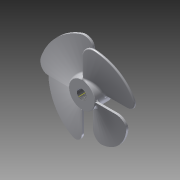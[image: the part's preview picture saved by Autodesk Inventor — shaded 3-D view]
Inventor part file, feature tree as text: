
AUTODESK INVENTOR PART (.ipt)
format: ipt  version: 2015 (Build 190159000, 159)  size: 707,584 bytes
history: native  units: mm
features: fillet x3, chamfer x2, sketch x2, extrude x1, helix x1, pattern_circular x1, hole x1, projected_geometry x1
ambient origin geometry x8: Origin, YZ Plane, XZ Plane, XY Plane, X Axis, Y Axis, Z Axis, Center Point
bodies: Solid1 (feature_tree)
feature tree (12):
  extrude  "Extrusion1"  Depth=40.0mm TaperAngle=0.0deg
  helix  "Coil1"  [1 undecoded]
  fillet  "Fillet1"  Radius=200.0mm
  fillet  "Fillet2"  Radius=2.0mm
  fillet  "Fillet3"  Radius=20.0mm
  chamfer  "Chamfer1"  Distance=4.0mm
  pattern_circular  "Circular Pattern1"  Angle=45.0deg  [1 undecoded]
  hole  "Hole1"  [1 undecoded]
  chamfer  "Chamfer2"  Distance=10.0mm
  sketch  "Sketch1"  dims[d0=60.0mm d1=40.0mm d2=0.0mm d3=5.0mm d4=200.0mm]
  sketch  "Sketch2"  dims[d5=100.0mm d6=10.0mm d7=2.5mm d8=0.0mm d9=90.0deg d10=90.0deg d11=0.0mm d12=0.0mm d13=2.0mm d14=20.0mm d15=4.0mm d16=1.0mm d17=2.0mm d18=45.0deg d19=40.0mm d20=360.0deg d22=10.0mm d23=10.0mm d24=22.835mm d25=50.0mm d26=4.0mm d27=2.0mm d28=90.0deg d29=59.3mm d30=20.594885mm d31=1.0mm d32=2.0mm d33=45.0deg]
  projected_geometry  "Projected Loop1"
note: 3 required parameter values undecoded (feature->parameter linkage not recoverable at this tier; creation-order binding heuristic only, values carry confidence <= 0.55)
